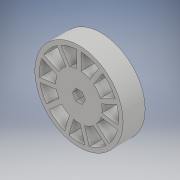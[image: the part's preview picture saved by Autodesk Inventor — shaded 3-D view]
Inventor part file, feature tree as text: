
AUTODESK INVENTOR PART (.ipt)
format: ipt  version: 2018 (Build 220112000, 112)  size: 268,800 bytes
history: native  units: in
note: dims shown in document units (in); Inventor stores cm internally (conversion verified against a paired STEP export)
features: extrude x3, sketch x3
ambient origin geometry x8: Origin, YZ Plane, XZ Plane, XY Plane, X Axis, Y Axis, Z Axis, Center Point
bodies: Body1 (feature_tree)
feature tree (6):
  extrude  "Extrusion3"  Depth=0.2in
  extrude  "Extrusion4"  Depth=0.75in
  extrude  "Extrusion5"  Depth=0.5in
  sketch  "Sketch1"  dims[d0=4.0in d1=0.2in]
  sketch  "Sketch3"  dims[d2=0.75in d3=0.3in]
  sketch  "Sketch4"  dims[d4=0.9in d5=0.5in d6=0.2in d7=0.1in d8=0.2in d9=0.2248in d10=0.4in d11=0.2248in d12=0.2in d13=0.3in d14=0.2in d15=0.2248in d16=0.35in d17=0.2248in d18=0.2in d19=0.2in d20=0.2248in d21=0.4in d22=0.2in d23=0.2in d24=0.2248in d25=0.3in d26=0.2in d27=0.2248in d28=0.35in d29=0.2in d30=0.2248in d31=0.3in d32=0.2in d33=0.2248in d34=0.375in d35=0.2in d36=0.2248in d37=0.35in d53=1.0in d54=0.0in d55=0.1in d56=0.0in d57=0.1in d62=0.1in d64=0.1in d66=0.1in d68=0.1in d70=0.0943in d72=0.0943in d73=0.0943in d74=0.0943in d75=0.0943in d76=0.0943in d77=0.0943in d78=0.1in d79=0.65in d80=0.0in]
